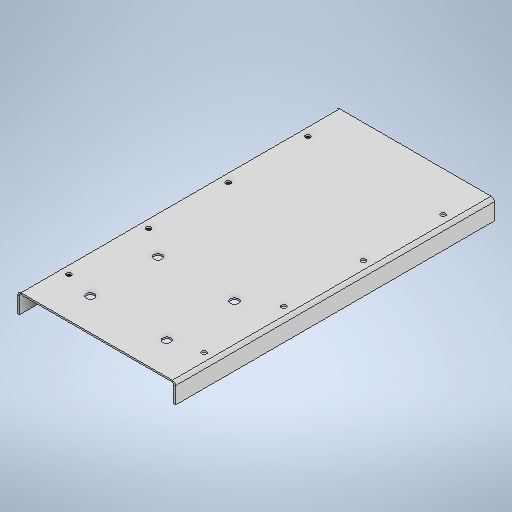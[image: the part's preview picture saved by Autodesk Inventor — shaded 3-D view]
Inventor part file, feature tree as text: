
AUTODESK INVENTOR PART (.ipt)
format: ipt  version: 2025 (Build 290162010, 162A)  size: 330,240 bytes
history: native  units: mm
features: sheet_metal_op x4, sketch x4, other x3, extrude x2, pattern_linear x1
ambient origin geometry x8: Origin, YZ Plane, XZ Plane, XY Plane, X Axis, Y Axis, Z Axis, Center Point
bodies: Body1 (feature_tree)
feature tree (14):
  sheet_metal_op  "Face2"
  extrude  "Extrusion2"  Depth=400.0mm
  sheet_metal_op  "Flange5"
  extrude  "Extrusion5"  Depth=10.0mm
  pattern_linear  "Rectangular Pattern2"  Spacing1=96.0mm  [1 undecoded]
  sketch  "Sketch4"  dims[d24=198.0mm d25=400.0mm]
  other  "Plate4"
  sketch  "Sketch7"  dims[d26=2.0mm d41=10.0mm]
  sketch  "Sketch9"  dims[d44=0.0mm d45=0.0mm]
  other  "Plate7"
  sheet_metal_op  "Bend5"
  sheet_metal_op  "Corner5"
  sketch  "Sketch12"  dims[d46=85.0mm d57=96.0mm d60=2.0mm d61=1.0mm d62=4.0mm d63=2.0mm d64=25.0mm d65=90.0deg d66=2.0mm d67=8.0mm d68=2.0mm d69=2.0mm d70=125.0mm d86=10.125mm d87=50.0mm d88=6.0mm d89=0.0mm d90=0.0mm d91=40.0mm d93=100.0mm d94=20.0mm d96=169.75mm d78=0.5mm d79=0.872665mm d80=0.5mm d81=0.872665mm]
  other  "Definition1"
note: 1 required parameter value undecoded (feature->parameter linkage not recoverable at this tier; creation-order binding heuristic only, values carry confidence <= 0.55)
